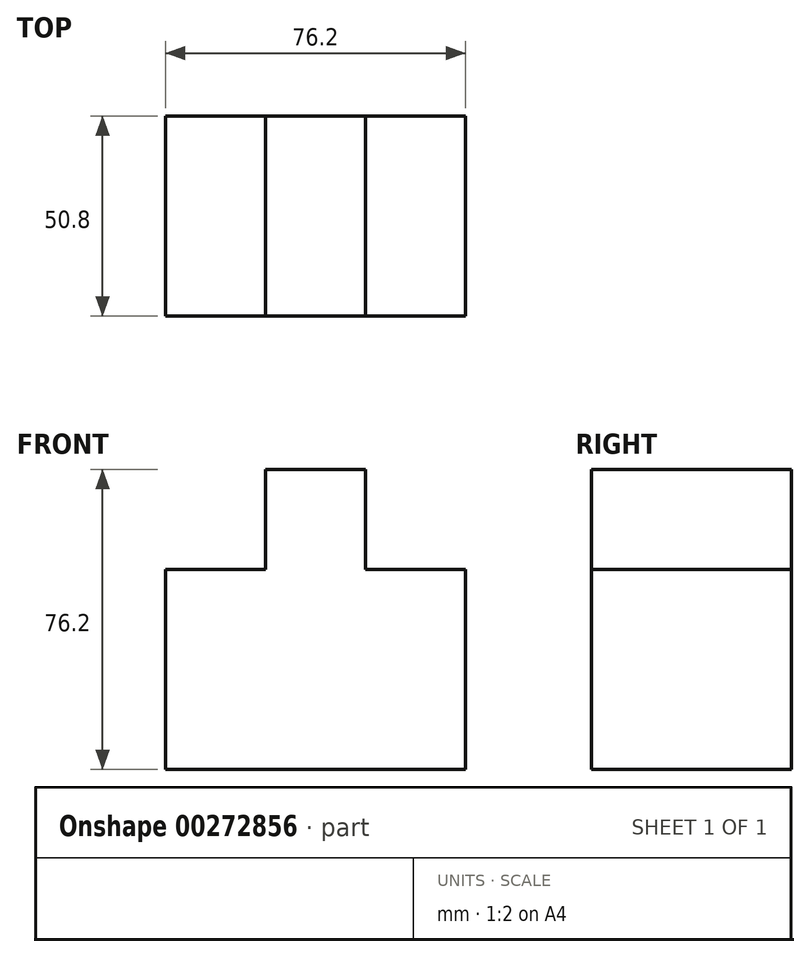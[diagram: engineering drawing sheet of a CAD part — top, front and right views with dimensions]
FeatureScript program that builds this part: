
annotation { "Feature Type Name" : "Feature", "Feature Type Description" : "" }
export const myFeature = defineFeature(function(context is Context, id is Id, definition is map)
    precondition{}
    {
        {
            var Q0;
            Q0=qCreatedBy(makeId("Front.planeOp"),FACE);
            var sketch = newSketch(context, id + "F0", { "sketchPlane" : qUnion([Q0])});
            skLineSegment(sketch, "E0", {"start": v(0, 0) * mm, "end": v(-76.2, 0) * mm});
            skLineSegment(sketch, "E1", {"start": v(0, 0) * mm, "end": v(0, 50.8) * mm});
            skLineSegment(sketch, "E2", {"start": v(-76.2, 0) * mm, "end": v(-76.2, 50.8) * mm});
            skLineSegment(sketch, "E3", {"start": v(-76.2, 50.8) * mm, "end": v(-50.8, 50.8) * mm});
            skLineSegment(sketch, "E4", {"start": v(-50.8, 50.8) * mm, "end": v(-50.8, 76.2) * mm});
            skLineSegment(sketch, "E5", {"start": v(-50.8, 76.2) * mm, "end": v(-25.4, 76.2) * mm});
            skLineSegment(sketch, "E6", {"start": v(-25.4, 76.2) * mm, "end": v(-25.4, 50.8) * mm});
            skLineSegment(sketch, "E7", {"start": v(-25.4, 50.8) * mm, "end": v(0, 50.8) * mm});
            skSolve(sketch);
        }
        {
            var Q0;
            Q0 = qSketchRegion(id + "F0", true);
            extrude(context, id + "F1", {"entities" : qUnion([Q0]), "depth" : 50.8 * mm});
        }
    });
